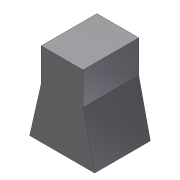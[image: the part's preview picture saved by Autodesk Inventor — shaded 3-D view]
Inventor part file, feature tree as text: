
AUTODESK INVENTOR PART (.ipt)
format: ipt  version: 2012 (Build 160160000, 160)  size: 83,456 bytes
history: native  units: in
note: dims shown in document units (in); Inventor stores cm internally (conversion verified against a paired STEP export)
features: extrude x2, sketch x2
ambient origin geometry x8: Origin, YZ Plane, XZ Plane, XY Plane, X Axis, Y Axis, Z Axis, Center Point
bodies: Solid1 (feature_tree)
feature tree (4):
  extrude  "Extrusion1"  Depth=14.0in
  extrude  "Extrusion2"  Depth=11.0in
  sketch  "Sketch1"  dims[d0=8.0in d1=0.0in d2=14.0in]
  sketch  "Sketch2"  dims[d3=18.0in d4=11.0in d5=9.0in d6=13.0in d7=0.0in]
